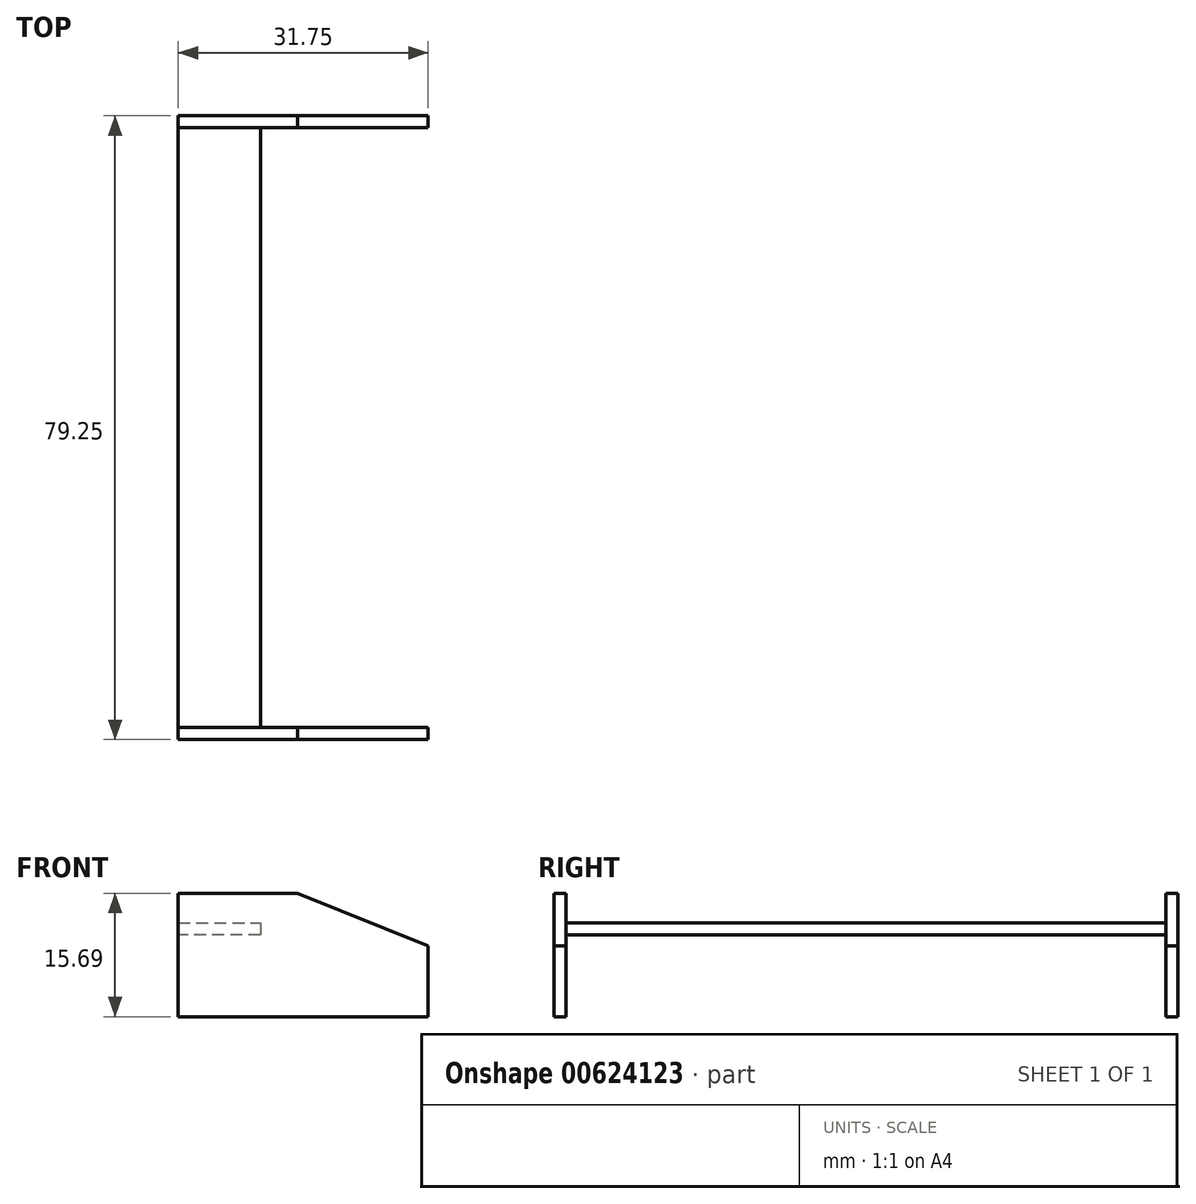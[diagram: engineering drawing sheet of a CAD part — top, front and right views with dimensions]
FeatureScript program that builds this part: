
annotation { "Feature Type Name" : "Feature", "Feature Type Description" : "" }
export const myFeature = defineFeature(function(context is Context, id is Id, definition is map)
    precondition{}
    {
        {
            var Q0;
            Q0=qCreatedBy(makeId("Front.planeOp"),FACE);
            var sketch = newSketch(context, id + "F0", { "sketchPlane" : qUnion([Q0])});
            skLineSegment(sketch, "E0", {"start": v(-13.4, 22.62) * mm, "end": v(-13.4, 6.93) * mm});
            skLineSegment(sketch, "E1", {"start": v(-13.4, 6.93) * mm, "end": v(18.35, 6.93) * mm});
            skLineSegment(sketch, "E2", {"start": v(18.35, 6.93) * mm, "end": v(18.35, 15.94) * mm});
            skLineSegment(sketch, "E3", {"start": v(18.35, 15.94) * mm, "end": v(1.76, 22.62) * mm});
            skLineSegment(sketch, "E4", {"start": v(1.76, 22.62) * mm, "end": v(-13.4, 22.62) * mm});
            skSolve(sketch);
        }
        {
            var Q0;
            Q0 = qSketchRegion(id + "F0", true);
            extrude(context, id + "F1", {"entities" : qUnion([Q0]), "endBound" : BoundingType.SYMMETRIC, "oppositeDirection" : true, "depth" : 1.52 * mm, "offsetDistance" : 25.4 * mm});
        }
        {
            var Q0;
            Q0=makeQuery(id+"F1.opExtrude","CAP_FACE",FACE,{"disambiguationData":[OSD([sQuery(id+"F0.wireOp",EDGE,"E0"),sQuery(id+"F0.wireOp",EDGE,"E1"),sQuery(id+"F0.wireOp",EDGE,"E2"),sQuery(id+"F0.wireOp",EDGE,"E3"),sQuery(id+"F0.wireOp",EDGE,"E4")])],"isStart":false});
            var sketch = newSketch(context, id + "F2", { "sketchPlane" : qUnion([Q0])});
            skLineSegment(sketch, "E5", {"start": v(13.4, 18.85) * mm, "end": v(2.97, 18.85) * mm});
            skLineSegment(sketch, "E6", {"start": v(2.97, 18.85) * mm, "end": v(2.97, 17.32) * mm});
            skLineSegment(sketch, "E7", {"start": v(2.97, 17.32) * mm, "end": v(13.4, 17.32) * mm});
            skSolve(sketch);
        }
        {
            var Q0;
            {var subQ0=sQuery(id+"F2.wireOp",EDGE,"E5");Q0=makeQuery(id+"F2.imprint","IMPRINT",FACE,{"disambiguationData":[TD([[makeQuery(id+"F2.imprint","IMPRINT",EDGE,{"derivedFrom":subQ0}),1.0]])]});}
            extrude(context, id + "F3", {"entities" : qUnion([Q0]), "operationType" : NewBodyOperationType.ADD, "depth" : 38.1 * mm, "offsetDistance" : 25.4 * mm});
        }
        {
            var Q0;
            Q0=makeQuery(id+"F3.opExtrude","CAP_FACE",FACE,{"disambiguationData":[OSD([sQuery(id+"F0.wireOp",EDGE,"E0"),sQuery(id+"F2.wireOp",EDGE,"E5"),sQuery(id+"F2.wireOp",EDGE,"E6"),sQuery(id+"F2.wireOp",EDGE,"E7")])],"isStart":false});
            cPlane(context, id + "F4", {"entities" : qUnion([Q0]), "cplaneType" : CPlaneType.OFFSET, "offset" : 0 * mm, "oppositeDirection" : true, "width" : 152.4 * mm, "height" : 152.4 * mm});
        }
        {
            var Q0;
            Q0=makeQuery(id+"F1.opExtrude","SWEPT_BODY",BODY,{"disambiguationData":[OSD([sQuery(id+"F0.wireOp",EDGE,"E0"),sQuery(id+"F0.wireOp",EDGE,"E1"),sQuery(id+"F0.wireOp",EDGE,"E2"),sQuery(id+"F0.wireOp",EDGE,"E3"),sQuery(id+"F0.wireOp",EDGE,"E4")])]});
            var Q1;
            Q1=qCreatedBy(id+"F4.planeOp",FACE);
            mirror(context, id + "F5", {"operationType" : NewBodyOperationType.ADD, "entities" : qUnion([Q0]), "mirrorPlane" : qUnion([Q1])});
        }
    });
